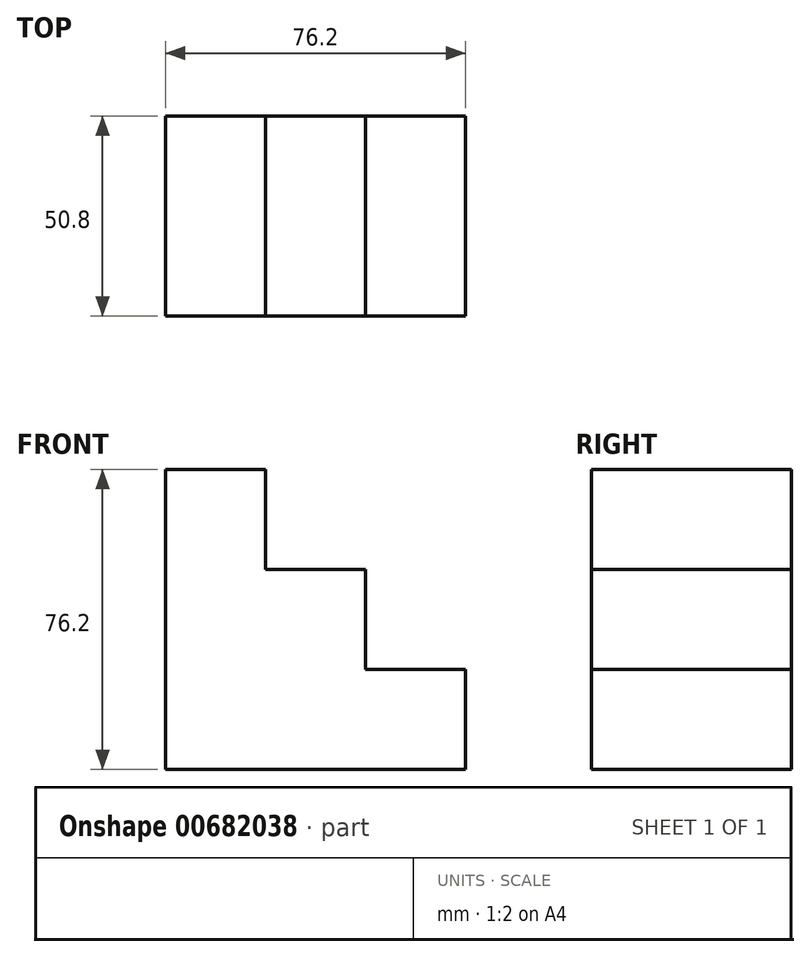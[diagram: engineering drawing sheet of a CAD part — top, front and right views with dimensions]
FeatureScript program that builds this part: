
annotation { "Feature Type Name" : "Feature", "Feature Type Description" : "" }
export const myFeature = defineFeature(function(context is Context, id is Id, definition is map)
    precondition{}
    {
        {
            var Q0;
            Q0=qCreatedBy(makeId("Front.planeOp"),FACE);
            var sketch = newSketch(context, id + "F0", { "sketchPlane" : qUnion([Q0])});
            skLineSegment(sketch, "E0", {"start": v(-56.05, 64.65) * mm, "end": v(-56.05, -11.55) * mm});
            skLineSegment(sketch, "E1", {"start": v(-56.05, -11.55) * mm, "end": v(20.15, -11.55) * mm});
            skLineSegment(sketch, "E2", {"start": v(-56.05, 64.65) * mm, "end": v(-30.65, 64.65) * mm});
            skLineSegment(sketch, "E3", {"start": v(-30.65, 64.65) * mm, "end": v(-30.65, 39.25) * mm});
            skLineSegment(sketch, "E4", {"start": v(-30.65, 39.25) * mm, "end": v(-5.25, 39.25) * mm});
            skLineSegment(sketch, "E5", {"start": v(-5.25, 39.25) * mm, "end": v(-5.25, 13.85) * mm});
            skLineSegment(sketch, "E6", {"start": v(-5.25, 13.85) * mm, "end": v(20.15, 13.85) * mm});
            skLineSegment(sketch, "E7", {"start": v(20.15, 13.85) * mm, "end": v(20.15, -11.55) * mm});
            skSolve(sketch);
        }
        {
            var Q0;
            Q0 = qSketchRegion(id + "F0", true);
            extrude(context, id + "F1", {"entities" : qUnion([Q0]), "depth" : 50.8 * mm, "offsetDistance" : 25.4 * mm});
        }
    });
